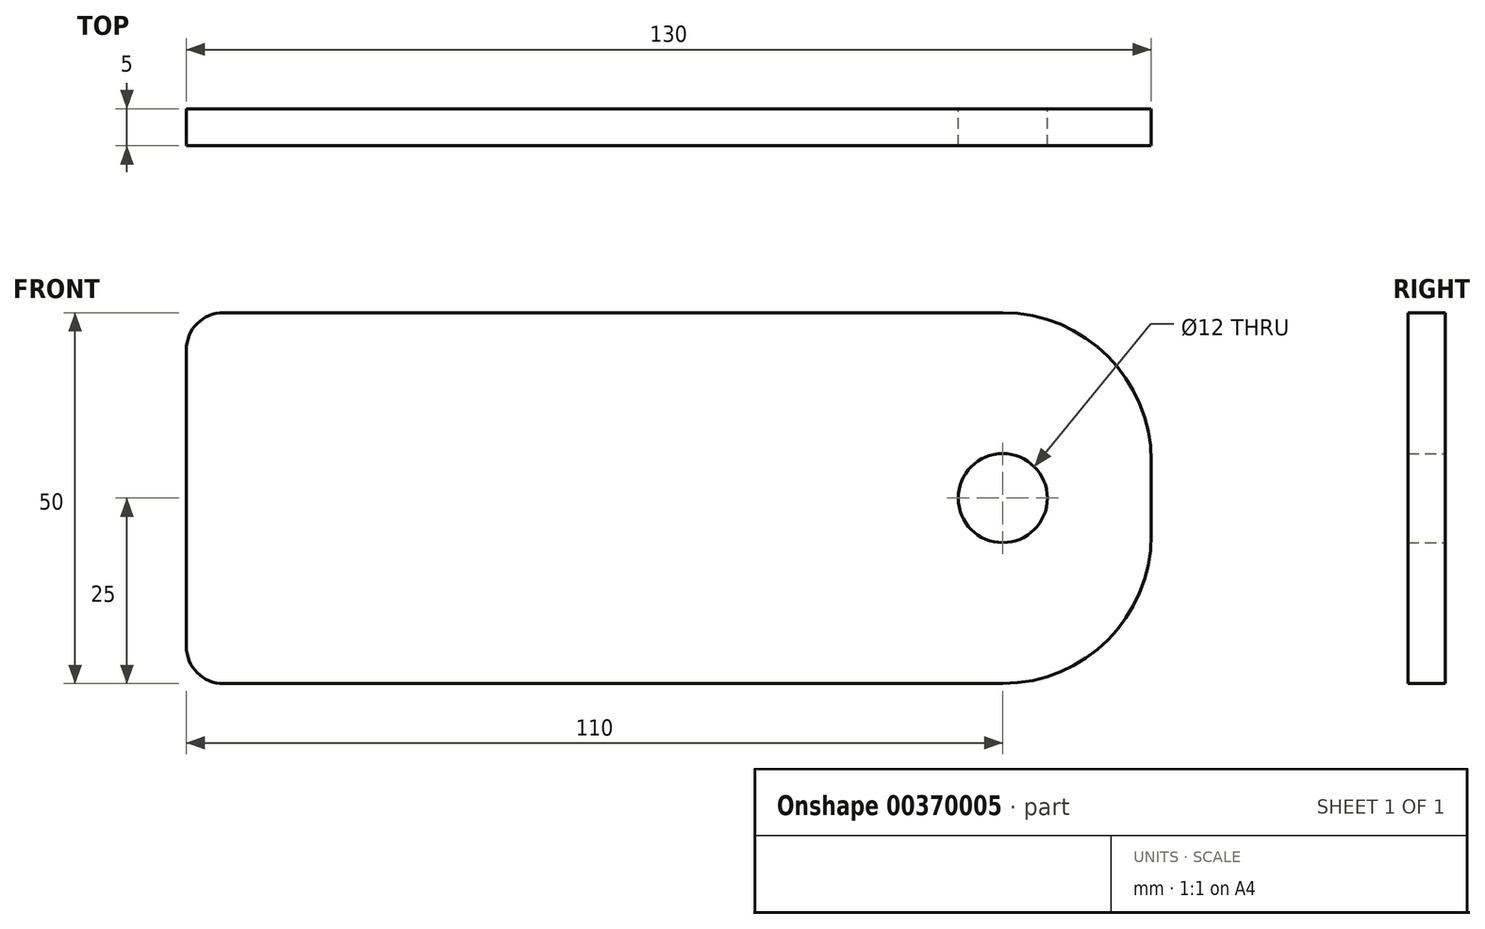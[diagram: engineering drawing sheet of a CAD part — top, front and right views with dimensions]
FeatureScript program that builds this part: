
annotation { "Feature Type Name" : "Feature", "Feature Type Description" : "" }
export const myFeature = defineFeature(function(context is Context, id is Id, definition is map)
    precondition{}
    {
        {
            var Q0;
            Q0=qCreatedBy(makeId("Front.planeOp"),FACE);
            var sketch = newSketch(context, id + "F0", { "sketchPlane" : qUnion([Q0])});
            skLineSegment(sketch, "E0.bottom", {"start": v(5, 0) * mm, "end": v(110, 0) * mm});
            skLineSegment(sketch, "E0.top", {"start": v(5, 50) * mm, "end": v(110, 50) * mm});
            skLineSegment(sketch, "E0.left", {"start": v(0, 5) * mm, "end": v(0, 45) * mm});
            skLineSegment(sketch, "E0.right", {"start": v(130, 20) * mm, "end": v(130, 30) * mm});
            skPoint(sketch, "E1.visualSharp", {"position": v(130, 50) * mm});
            skArc(sketch, "E1.filletArc", {"start": v(130, 30) * mm, "mid": v(124.14, 44.14) * mm, "end": v(110, 50) * mm});
            skPoint(sketch, "E2.visualSharp", {"position": v(130, 0) * mm});
            skArc(sketch, "E2.filletArc", {"start": v(110, 0) * mm, "mid": v(124.14, 5.86) * mm, "end": v(130, 20) * mm});
            skPoint(sketch, "E3.visualSharp", {"position": v(0, 50) * mm});
            skArc(sketch, "E3.filletArc", {"start": v(5, 50) * mm, "mid": v(1.46, 48.54) * mm, "end": v(0, 45) * mm});
            skPoint(sketch, "E4.visualSharp", {"position": v(0, 0) * mm});
            skArc(sketch, "E4.filletArc", {"start": v(0, 5) * mm, "mid": v(1.46, 1.46) * mm, "end": v(5, 0) * mm});
            skPoint(sketch, "E5", {"position": v(110, 25) * mm});
            skPoint(sketch, "E5.positionSnap0", {"position": v(0, 25) * mm});
            skCircle(sketch, "E6", {"center": v(110, 25) * mm, "radius": 6 * mm});
            skSolve(sketch);
        }
        {
            var Q0;
            Q0 = qSketchRegion(id + "F0", true);
            extrude(context, id + "F1", {"entities" : qUnion([Q0]), "depth" : 5 * mm});
        }
    });
